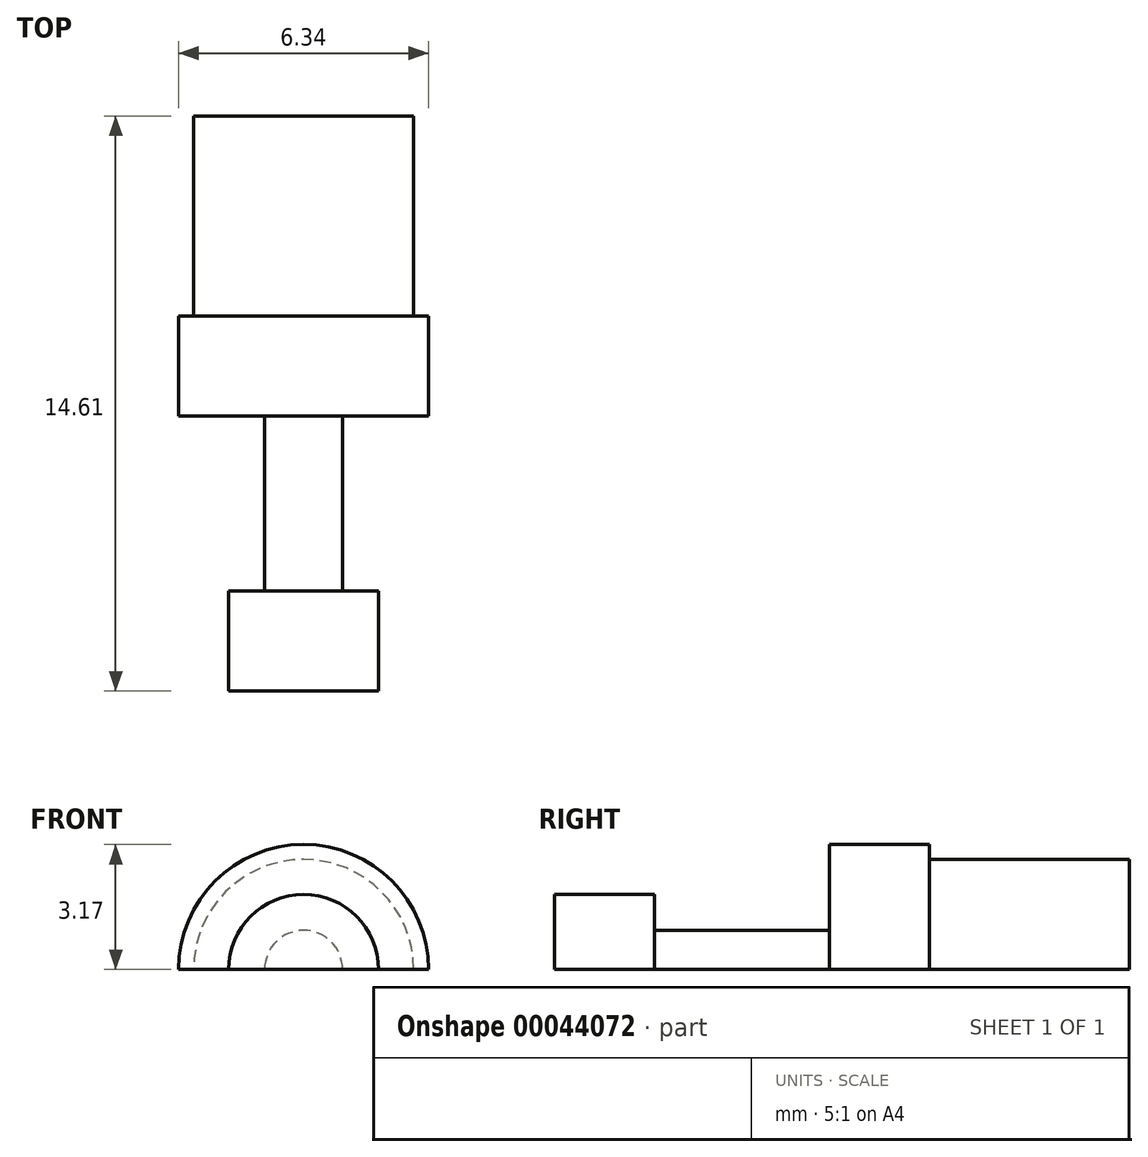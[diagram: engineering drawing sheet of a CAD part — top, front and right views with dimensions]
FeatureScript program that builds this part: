
annotation { "Feature Type Name" : "Feature", "Feature Type Description" : "" }
export const myFeature = defineFeature(function(context is Context, id is Id, definition is map)
    precondition{}
    {
        {
            var Q0;
            Q0=qCreatedBy(makeId("Right.planeOp"),FACE);
            var sketch = newSketch(context, id + "F0", { "sketchPlane" : qUnion([Q0])});
            skLineSegment(sketch, "E0", {"start": v(0, 0) * mm, "end": v(-14.6, 0) * mm});
            skLineSegment(sketch, "E1", {"start": v(-14.6, 0) * mm, "end": v(-14.6, 1.9) * mm});
            skLineSegment(sketch, "E2", {"start": v(-14.6, 1.9) * mm, "end": v(-12.06, 1.9) * mm});
            skLineSegment(sketch, "E3", {"start": v(-12.06, 1.9) * mm, "end": v(-12.06, 1) * mm});
            skLineSegment(sketch, "E4", {"start": v(-12.06, 1) * mm, "end": v(-7.62, 1) * mm});
            skLineSegment(sketch, "E5", {"start": v(-7.62, 1) * mm, "end": v(-7.62, 3.17) * mm});
            skLineSegment(sketch, "E6", {"start": v(-7.62, 3.17) * mm, "end": v(-5.08, 3.17) * mm});
            skLineSegment(sketch, "E7", {"start": v(-5.08, 3.17) * mm, "end": v(-5.08, 2.8) * mm});
            skLineSegment(sketch, "E8", {"start": v(-5.08, 2.8) * mm, "end": v(0, 2.8) * mm});
            skLineSegment(sketch, "E9", {"start": v(0, 2.8) * mm, "end": v(0, 0) * mm});
            skSolve(sketch);
        }
        {
            var Q0;
            Q0=makeQuery(id+"F0.imprint","IMPRINT",FACE,{"disambiguationData":[TD([[makeQuery(id+"F0.imprint","IMPRINT",EDGE,{"derivedFrom":sQuery(id+"F0.wireOp",EDGE,"E0")}),-1.0]])]});
            var Q1;
            Q1=sQuery(id+"F0.wireOp",EDGE,"E0");
            revolve(context, id + "F1", {"entities" : qUnion([Q0]), "axis" : qUnion([Q1]), "revolveType" : RevolveType.SYMMETRIC, "angle" : 180 * degree});
        }
    });
